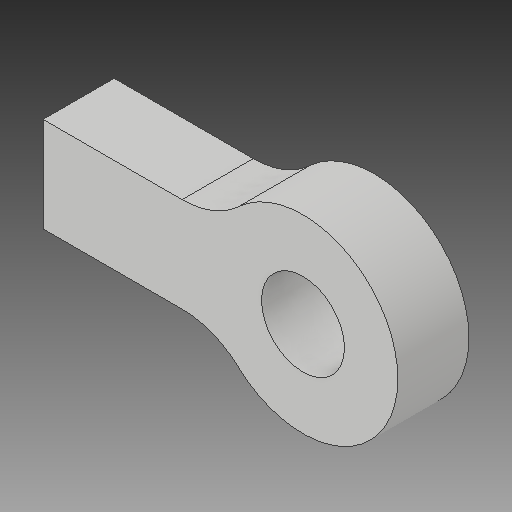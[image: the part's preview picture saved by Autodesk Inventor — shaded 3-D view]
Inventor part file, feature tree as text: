
AUTODESK INVENTOR PART (.ipt)
format: ipt  version: 2019 (Build 230136000, 136)  size: 109,568 bytes
history: native  units: mm
features: extrude x1, fillet x1, sketch x1
ambient origin geometry x8: Origin, YZ Plane, XZ Plane, XY Plane, X Axis, Y Axis, Z Axis, Center Point
bodies: Solid1 (feature_tree)
feature tree (3):
  extrude  "Extrusion1"  Depth=7.0mm
  fillet  "Fillet1"  Radius=8.0mm
  sketch  "Sketch1"  dims[d0=8.0mm d1=15.0mm d2=8.0mm d3=15.0mm d5=7.0mm d6=6.0mm d7=0.0mm d8=7.0mm]
